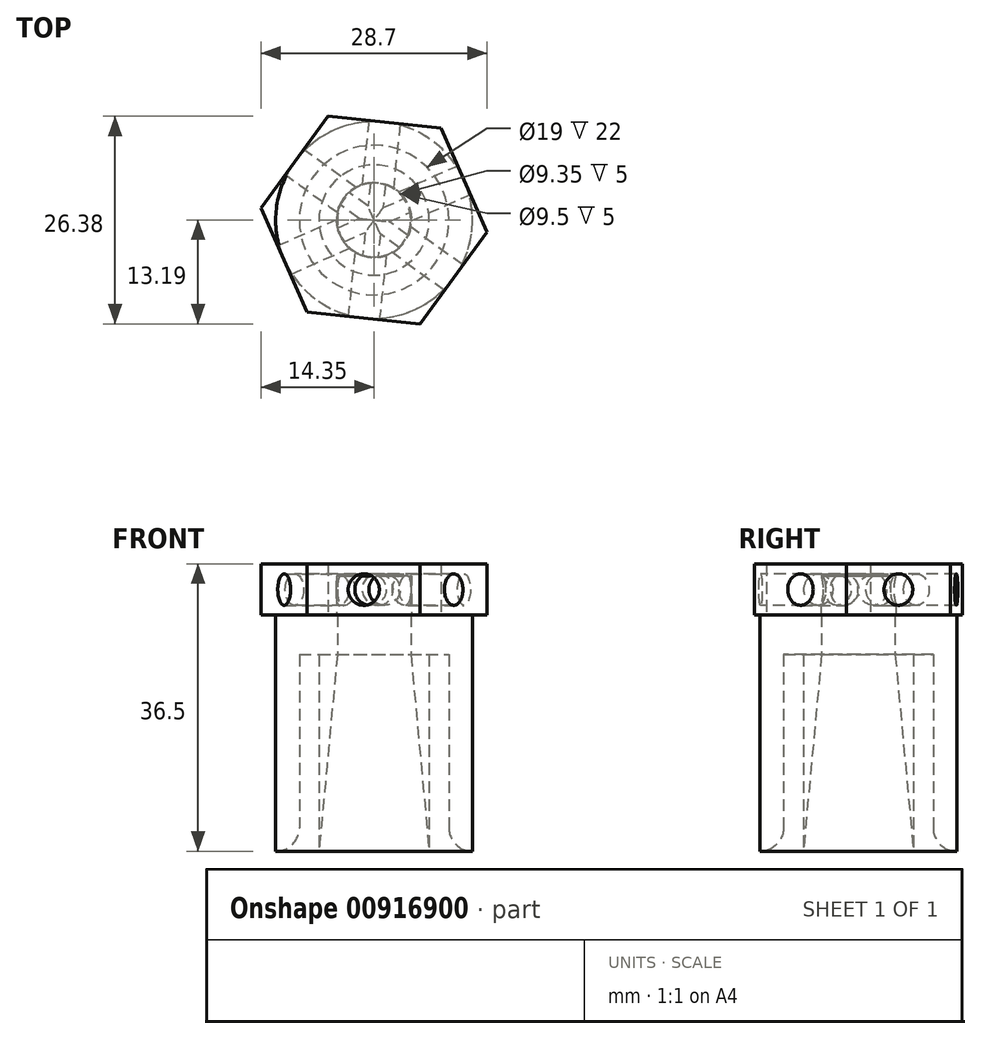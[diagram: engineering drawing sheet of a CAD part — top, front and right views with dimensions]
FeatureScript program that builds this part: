
annotation { "Feature Type Name" : "Feature", "Feature Type Description" : "" }
export const myFeature = defineFeature(function(context is Context, id is Id, definition is map)
    precondition{}
    {
        {
            var Q0;
            Q0=qCreatedBy(makeId("Front.planeOp"),FACE);
            var sketch = newSketch(context, id + "F0", { "sketchPlane" : qUnion([Q0])});
            skLineSegment(sketch, "E0.bottom", {"start": v(12.5, 0) * mm, "end": v(12.5, 0) * mm});
            skLineSegment(sketch, "E0.left", {"start": v(9.5, 3) * mm, "end": v(9.5, 25) * mm});
            skLineSegment(sketch, "E0.right", {"start": v(12.5, 0) * mm, "end": v(12.5, 25) * mm});
            skLineSegment(sketch, "E1", {"start": v(12.5, 25) * mm, "end": v(12.5, 30) * mm});
            skLineSegment(sketch, "E2", {"start": v(0, 0) * mm, "end": v(0, 55.26) * mm});
            skPoint(sketch, "E3.visualSharp", {"position": v(9.5, 0) * mm});
            skArc(sketch, "E3.filletArc", {"start": v(9.5, 3) * mm, "mid": v(10.38, 0.88) * mm, "end": v(12.5, 0) * mm});
            skLineSegment(sketch, "E4", {"start": v(9.5, 25) * mm, "end": v(7, 25) * mm});
            skLineSegment(sketch, "E5", {"start": v(7, 0) * mm, "end": v(7, 25) * mm});
            skLineSegment(sketch, "E6", {"start": v(4.67, 25) * mm, "end": v(7, 0) * mm});
            skLineSegment(sketch, "E7", {"start": v(4.67, 25) * mm, "end": v(4.67, 30) * mm});
            skLineSegment(sketch, "E8", {"start": v(12.5, 30) * mm, "end": v(4.67, 30) * mm});
            skSolve(sketch);
        }
        {
            var Q0;
            Q0 = qSketchRegion(id + "F0", true);
            var Q1;
            Q1=sQuery(id+"F0.wireOp",EDGE,"E2");
            revolve(context, id + "F1", {"surfaceOperationType" : NewSurfaceOperationType.NEW, "entities" : qUnion([Q0]), "axis" : qUnion([Q1]), "revolveType" : RevolveType.FULL});
        }
        {
            var Q0;
            Q0=makeQuery(id+"F1.opRevolve","SWEPT_FACE",FACE,{"disambiguationData":[OSD([sQuery(id+"F0.wireOp",EDGE,"E8")])]});
            var sketch = newSketch(context, id + "F2", { "sketchPlane" : qUnion([Q0])});
            skCircle(sketch, "E9.cCircle", {"center": v(0, 0) * mm, "radius": 12.5 * mm, "construction": true});
            skPoint(sketch, "E9.0.midPoint", {"position": v(-5.97, 10.98) * mm});
            skCircle(sketch, "E10", {"center": v(0, 0) * mm, "radius": 4.75 * mm});
            skLineSegment(sketch, "E11.0", {"start": v(5.86, -13.19) * mm, "end": v(-8.5, -11.67) * mm});
            skLineSegment(sketch, "E11.1", {"start": v(-8.5, -11.67) * mm, "end": v(-14.35, 1.52) * mm});
            skLineSegment(sketch, "E11.2", {"start": v(-14.35, 1.52) * mm, "end": v(-5.86, 13.19) * mm});
            skLineSegment(sketch, "E11.3", {"start": v(-5.86, 13.19) * mm, "end": v(8.5, 11.67) * mm});
            skLineSegment(sketch, "E11.4", {"start": v(8.5, 11.67) * mm, "end": v(14.35, -1.52) * mm});
            skLineSegment(sketch, "E11.5", {"start": v(14.35, -1.52) * mm, "end": v(5.86, -13.19) * mm});
            skPoint(sketch, "E11.0.midPoint", {"position": v(-1.32, -12.43) * mm});
            skSolve(sketch);
        }
        {
            var Q0;
            Q0 = qSketchRegion(id + "F2", true);
            extrude(context, id + "F3", {"entities" : qUnion([Q0]), "operationType" : NewBodyOperationType.ADD, "depth" : 5 * mm, "offsetDistance" : 25 * mm});
        }
        {
            var Q0;
            Q0=makeQuery(id+"F3.opExtrude","CAP_FACE",FACE,{"disambiguationData":[OSD([sQuery(id+"F2.wireOp",EDGE,"E10"),sQuery(id+"F2.wireOp",EDGE,"E11.0"),sQuery(id+"F2.wireOp",EDGE,"E11.1"),sQuery(id+"F2.wireOp",EDGE,"E11.2"),sQuery(id+"F2.wireOp",EDGE,"E11.3"),sQuery(id+"F2.wireOp",EDGE,"E11.4"),sQuery(id+"F2.wireOp",EDGE,"E11.5")])],"isStart":false});
            var sketch = newSketch(context, id + "F4", { "sketchPlane" : qUnion([Q0])});
            skCircle(sketch, "E12.cCircle", {"center": v(0, 0) * mm, "radius": 12.5 * mm, "construction": true});
            skLineSegment(sketch, "E12.0", {"start": v(-14.35, 1.52) * mm, "end": v(-5.86, 13.19) * mm});
            skLineSegment(sketch, "E12.1", {"start": v(-5.86, 13.19) * mm, "end": v(8.5, 11.67) * mm});
            skLineSegment(sketch, "E12.2", {"start": v(8.5, 11.67) * mm, "end": v(14.35, -1.52) * mm});
            skLineSegment(sketch, "E12.3", {"start": v(14.35, -1.52) * mm, "end": v(5.86, -13.19) * mm});
            skLineSegment(sketch, "E12.4", {"start": v(5.86, -13.19) * mm, "end": v(-8.5, -11.67) * mm});
            skLineSegment(sketch, "E12.5", {"start": v(-8.5, -11.67) * mm, "end": v(-14.35, 1.52) * mm});
            skPoint(sketch, "E12.0.midPoint", {"position": v(-10.1, 7.35) * mm});
            skSolve(sketch);
        }
        {
            var Q0;
            Q0 = qSketchRegion(id + "F4", true);
            extrude(context, id + "F5", {"entities" : qUnion([Q0]), "operationType" : NewBodyOperationType.ADD, "depth" : 1.5 * mm, "offsetDistance" : 25 * mm});
        }
        {
            var Q0;
            Q0=makeQuery(id+"F5.boolean.opBoolean","MERGE",FACE,{"derivedFrom":[makeQuery(id+"F3.opExtrude","SWEPT_FACE",FACE,{"disambiguationData":[OSD([sQuery(id+"F2.wireOp",EDGE,"E11.0")])]}),makeQuery(id+"F5.opExtrude","SWEPT_FACE",FACE,{"disambiguationData":[OSD([sQuery(id+"F4.wireOp",EDGE,"E12.4")])]})]});
            var sketch = newSketch(context, id + "F6", { "sketchPlane" : qUnion([Q0])});
            skLineSegment(sketch, "E13", {"start": v(0, 36.5) * mm, "end": v(0, 30) * mm, "construction": true});
            skLineSegment(sketch, "E14", {"start": v(-7.22, 33.25) * mm, "end": v(7.22, 33.25) * mm, "construction": true});
            skCircle(sketch, "E15", {"center": v(0, 33.25) * mm, "radius": 2 * mm});
            skSolve(sketch);
        }
        {
            var Q0;
            Q0 = qSketchRegion(id + "F6", true);
            extrude(context, id + "F7", {"entities" : qUnion([Q0]), "operationType" : NewBodyOperationType.REMOVE, "oppositeDirection" : true, "depth" : 30 * mm, "offsetDistance" : 25 * mm});
        }
        {
            var Q0;
            Q0=makeQuery(id+"F5.boolean.opBoolean","MERGE",FACE,{"derivedFrom":[makeQuery(id+"F3.opExtrude","SWEPT_FACE",FACE,{"disambiguationData":[OSD([sQuery(id+"F2.wireOp",EDGE,"E11.2")])]}),makeQuery(id+"F5.opExtrude","SWEPT_FACE",FACE,{"disambiguationData":[OSD([sQuery(id+"F4.wireOp",EDGE,"E12.0")])]})]});
            var sketch = newSketch(context, id + "F8", { "sketchPlane" : qUnion([Q0])});
            skLineSegment(sketch, "E16", {"start": v(0, 36.5) * mm, "end": v(0, 30) * mm, "construction": true});
            skLineSegment(sketch, "E17", {"start": v(7.22, 33.25) * mm, "end": v(-7.22, 33.25) * mm, "construction": true});
            skCircle(sketch, "E18", {"center": v(0, 33.25) * mm, "radius": 2 * mm});
            skSolve(sketch);
        }
        {
            var Q0;
            Q0 = qSketchRegion(id + "F8", true);
            extrude(context, id + "F9", {"entities" : qUnion([Q0]), "operationType" : NewBodyOperationType.REMOVE, "oppositeDirection" : true, "depth" : 30 * mm, "offsetDistance" : 25 * mm});
        }
        {
            var Q0;
            Q0=makeQuery(id+"F5.boolean.opBoolean","MERGE",FACE,{"derivedFrom":[makeQuery(id+"F3.opExtrude","SWEPT_FACE",FACE,{"disambiguationData":[OSD([sQuery(id+"F2.wireOp",EDGE,"E11.4")])]}),makeQuery(id+"F5.opExtrude","SWEPT_FACE",FACE,{"disambiguationData":[OSD([sQuery(id+"F4.wireOp",EDGE,"E12.2")])]})]});
            var sketch = newSketch(context, id + "F10", { "sketchPlane" : qUnion([Q0])});
            skLineSegment(sketch, "E19", {"start": v(0, 36.5) * mm, "end": v(0, 30) * mm, "construction": true});
            skLineSegment(sketch, "E20", {"start": v(-7.22, 33.25) * mm, "end": v(7.22, 33.25) * mm, "construction": true});
            skCircle(sketch, "E21", {"center": v(0, 33.25) * mm, "radius": 2 * mm});
            skSolve(sketch);
        }
        {
            var Q0;
            Q0 = qSketchRegion(id + "F10", true);
            extrude(context, id + "F11", {"entities" : qUnion([Q0]), "operationType" : NewBodyOperationType.REMOVE, "oppositeDirection" : true, "depth" : 30 * mm, "offsetDistance" : 25 * mm});
        }
    });
